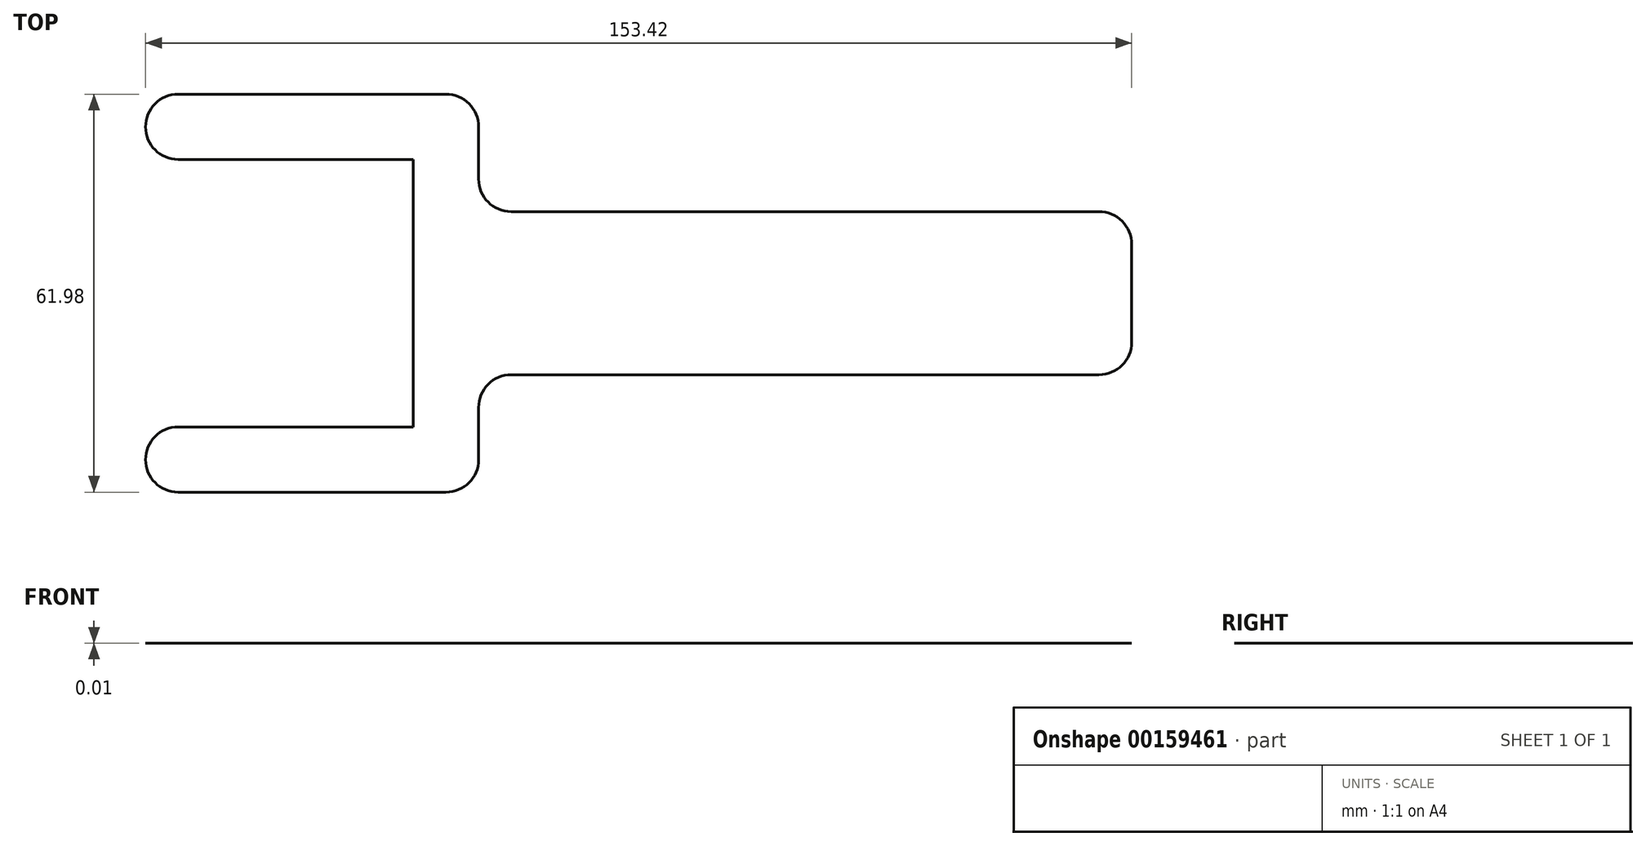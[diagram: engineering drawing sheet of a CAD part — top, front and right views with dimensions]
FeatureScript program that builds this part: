
annotation { "Feature Type Name" : "Feature", "Feature Type Description" : "" }
export const myFeature = defineFeature(function(context is Context, id is Id, definition is map)
    precondition{}
    {
        {
            var Q0;
            Q0=qCreatedBy(makeId("Top.planeOp"),FACE);
            var sketch = newSketch(context, id + "F0", { "sketchPlane" : qUnion([Q0])});
            skLineSegment(sketch, "E0", {"start": v(0, 0) * mm, "end": v(41.66, 0) * mm});
            skLineSegment(sketch, "E1", {"start": v(41.66, 0) * mm, "end": v(41.66, 41.66) * mm});
            skLineSegment(sketch, "E2", {"start": v(41.66, 41.66) * mm, "end": v(0, 41.66) * mm});
            skLineSegment(sketch, "E3", {"start": v(0, 51.82) * mm, "end": v(51.82, 51.82) * mm});
            skLineSegment(sketch, "E4", {"start": v(51.82, -10.16) * mm, "end": v(0, -10.16) * mm});
            skLineSegment(sketch, "E5", {"start": v(0, -10.16) * mm, "end": v(0, 0) * mm});
            skLineSegment(sketch, "E6", {"start": v(0, 41.66) * mm, "end": v(0, 51.82) * mm});
            skLineSegment(sketch, "E7", {"start": v(51.82, 51.82) * mm, "end": v(51.82, 33.53) * mm});
            skLineSegment(sketch, "E8", {"start": v(51.82, 33.53) * mm, "end": v(153.42, 33.53) * mm});
            skLineSegment(sketch, "E9", {"start": v(153.42, 33.53) * mm, "end": v(153.42, 8.13) * mm});
            skLineSegment(sketch, "E10", {"start": v(153.42, 8.13) * mm, "end": v(51.82, 8.13) * mm});
            skLineSegment(sketch, "E11", {"start": v(51.82, 8.13) * mm, "end": v(51.82, -10.16) * mm});
            skSolve(sketch);
        }
        {
            var Q0;
            Q0=makeQuery(id+"F0.imprint","IMPRINT",FACE,{"disambiguationData":[TD([[makeQuery(id+"F0.imprint","IMPRINT",EDGE,{"derivedFrom":sQuery(id+"F0.wireOp",EDGE,"E0")}),-1.0]])]});
            extrude(context, id + "F1", {"entities" : qUnion([Q0]), "depth" : 3 / 406.4 * mm});
        }
        {
            var Q0;
            Q0=makeQuery(id+"F1.opExtrude","SWEPT_EDGE",EDGE,{"disambiguationData":[OSD([sQuery(id+"F0.wireOp",EDGE,"E2"),sQuery(id+"F0.wireOp",EDGE,"E6")])]});
            var Q1;
            Q1=makeQuery(id+"F1.opExtrude","SWEPT_EDGE",EDGE,{"disambiguationData":[OSD([sQuery(id+"F0.wireOp",EDGE,"E3"),sQuery(id+"F0.wireOp",EDGE,"E6")])]});
            var Q2;
            Q2=makeQuery(id+"F1.opExtrude","SWEPT_EDGE",EDGE,{"disambiguationData":[OSD([sQuery(id+"F0.wireOp",EDGE,"E0"),sQuery(id+"F0.wireOp",EDGE,"E5")])]});
            var Q3;
            Q3=makeQuery(id+"F1.opExtrude","SWEPT_EDGE",EDGE,{"disambiguationData":[OSD([sQuery(id+"F0.wireOp",EDGE,"E4"),sQuery(id+"F0.wireOp",EDGE,"E5")])]});
            var Q4;
            Q4=makeQuery(id+"F1.opExtrude","SWEPT_EDGE",EDGE,{"disambiguationData":[OSD([sQuery(id+"F0.wireOp",EDGE,"E4"),sQuery(id+"F0.wireOp",EDGE,"E11")])]});
            var Q5;
            Q5=makeQuery(id+"F1.opExtrude","SWEPT_EDGE",EDGE,{"disambiguationData":[OSD([sQuery(id+"F0.wireOp",EDGE,"E10"),sQuery(id+"F0.wireOp",EDGE,"E11")])]});
            var Q6;
            Q6=makeQuery(id+"F1.opExtrude","SWEPT_EDGE",EDGE,{"disambiguationData":[OSD([sQuery(id+"F0.wireOp",EDGE,"E7"),sQuery(id+"F0.wireOp",EDGE,"E8")])]});
            var Q7;
            Q7=makeQuery(id+"F1.opExtrude","SWEPT_EDGE",EDGE,{"disambiguationData":[OSD([sQuery(id+"F0.wireOp",EDGE,"E3"),sQuery(id+"F0.wireOp",EDGE,"E7")])]});
            var Q8;
            Q8=makeQuery(id+"F1.opExtrude","SWEPT_EDGE",EDGE,{"disambiguationData":[OSD([sQuery(id+"F0.wireOp",EDGE,"E8"),sQuery(id+"F0.wireOp",EDGE,"E9")])]});
            var Q9;
            Q9=makeQuery(id+"F1.opExtrude","SWEPT_EDGE",EDGE,{"disambiguationData":[OSD([sQuery(id+"F0.wireOp",EDGE,"E9"),sQuery(id+"F0.wireOp",EDGE,"E10")])]});
            fillet(context, id + "F2", {"entities" : qUnion([Q0, Q1, Q2, Q3, Q4, Q5, Q6, Q7, Q8, Q9]), "radius" : 5.08 * mm, "tangentPropagation" : true, "allowEdgeOverflow" : false});
        }
    });
